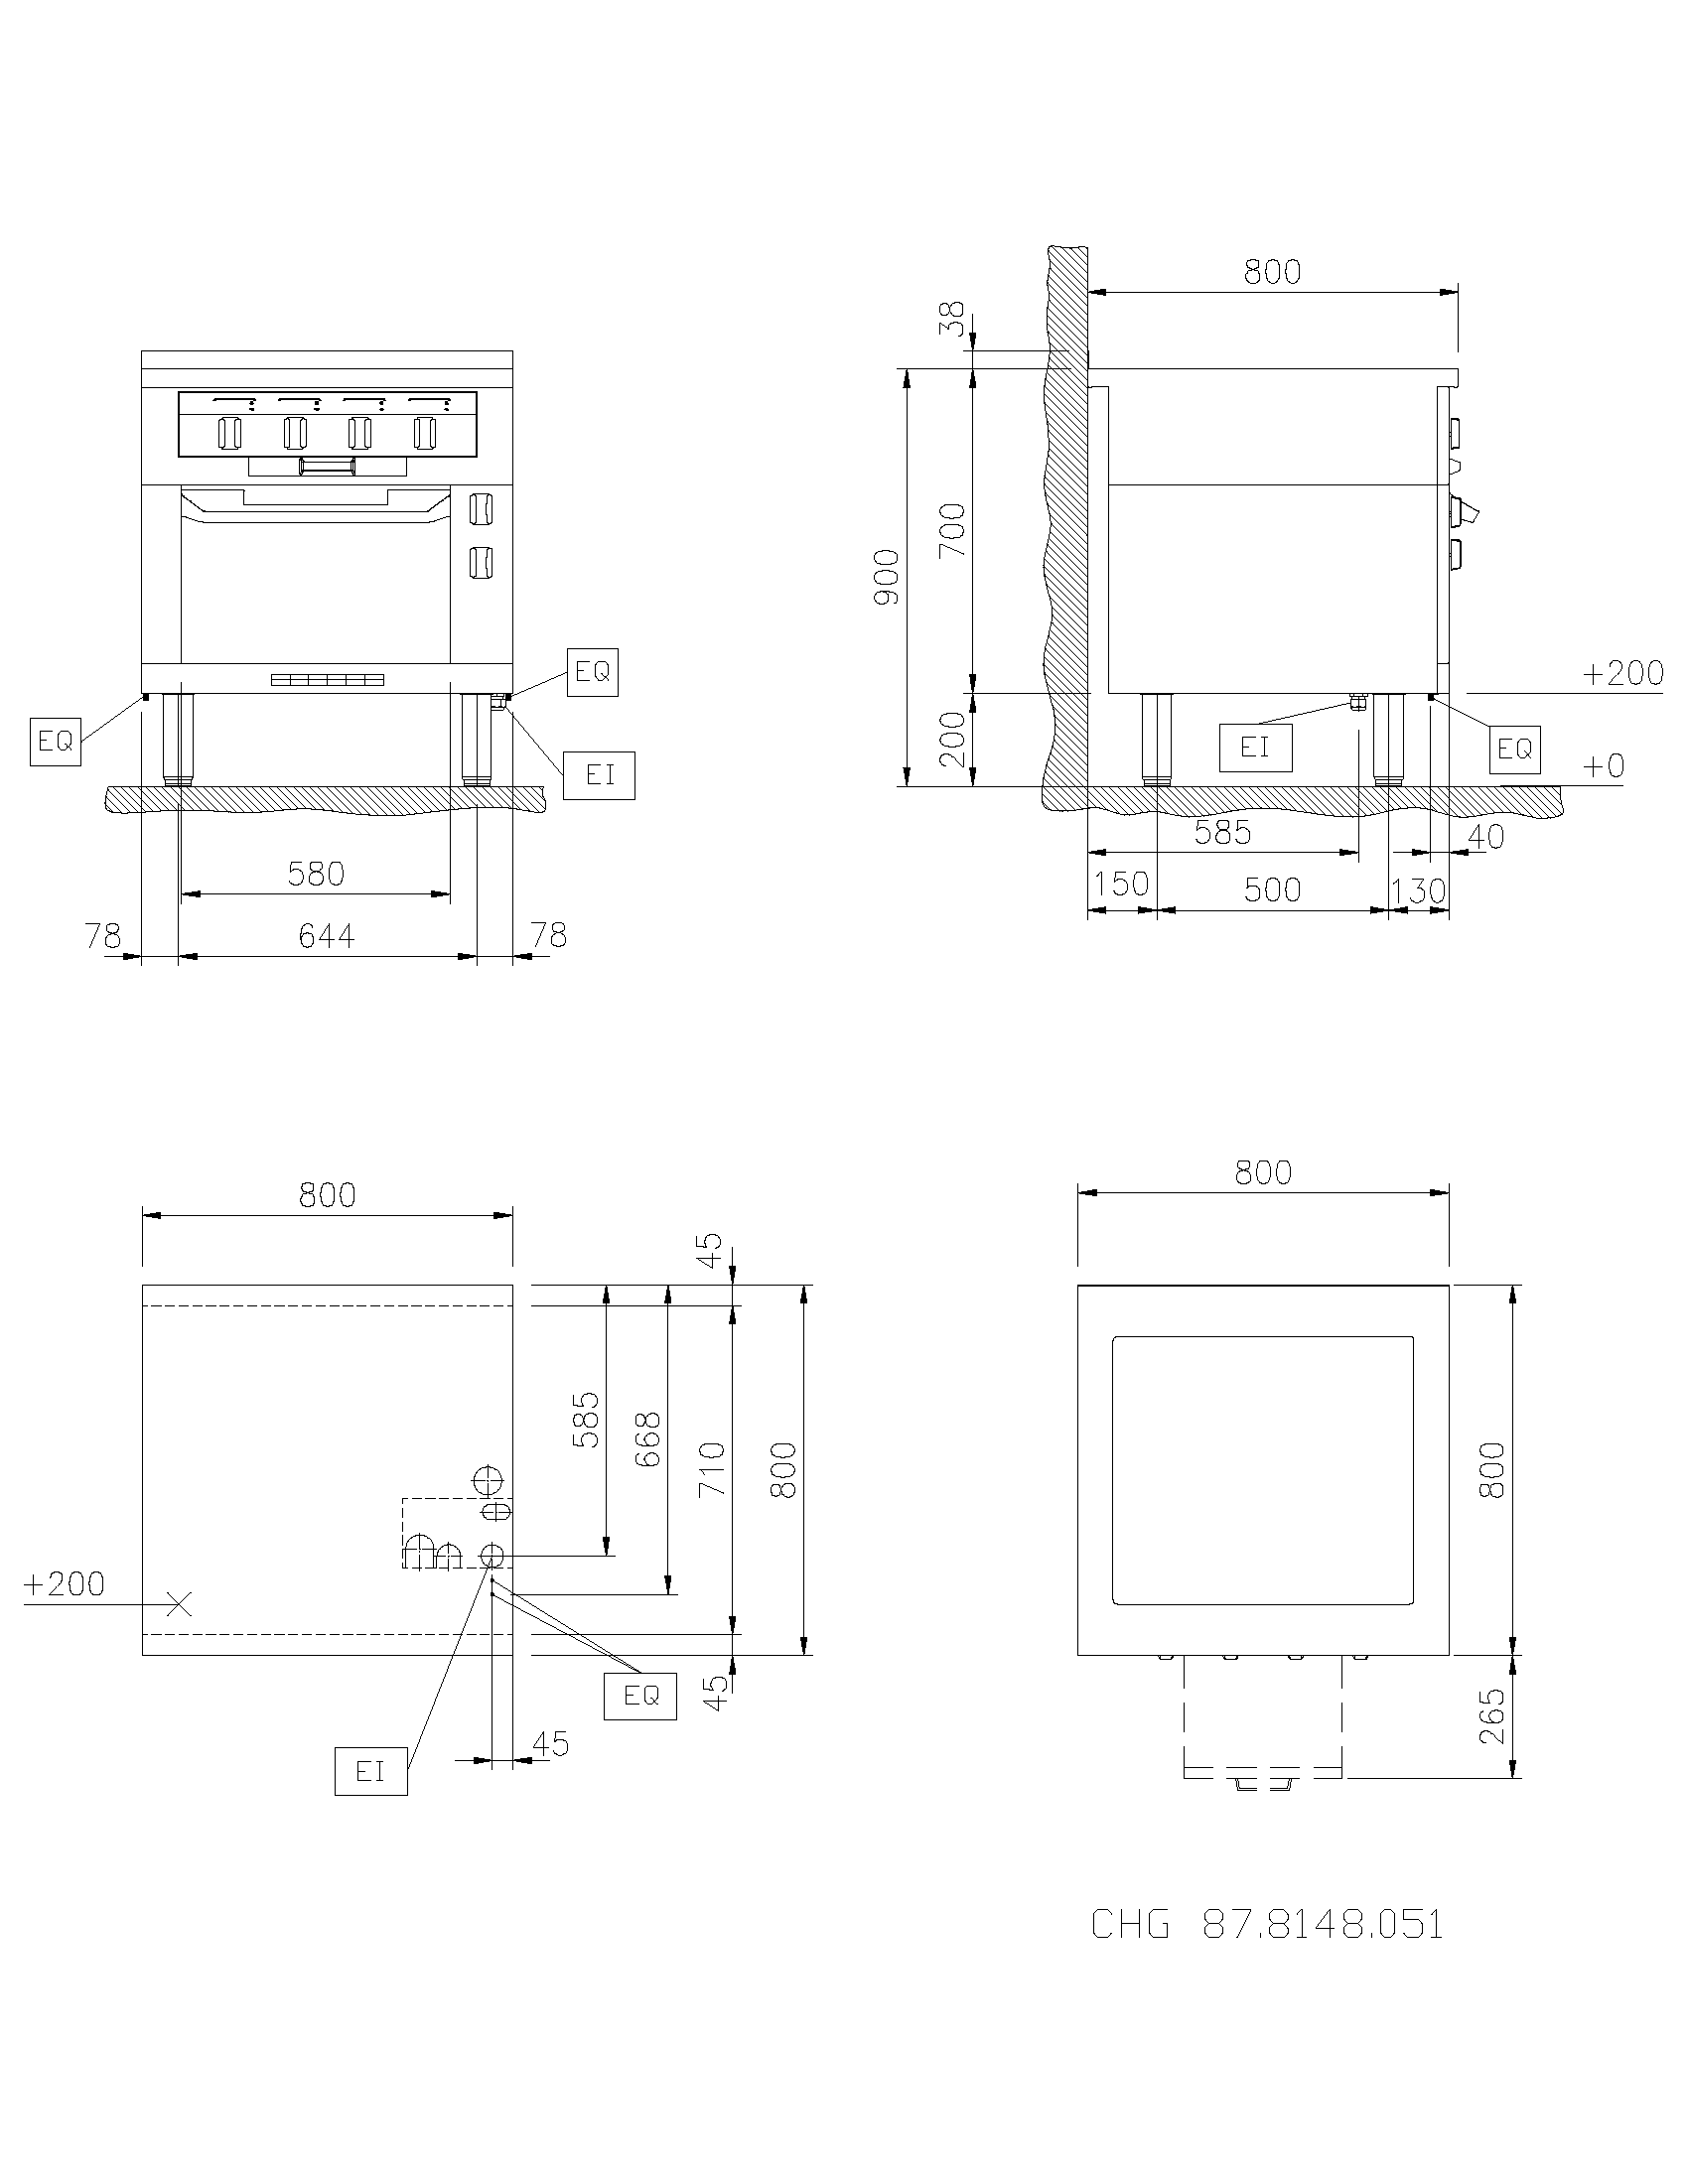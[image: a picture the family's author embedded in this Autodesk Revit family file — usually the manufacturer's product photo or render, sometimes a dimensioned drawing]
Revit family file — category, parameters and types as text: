
# Revit family: QF_ELECTROLUXPROFESSIONAL_588459_MALRECH4AO
name_source: partatom
category: Attrezzature speciali
units: mm (PartAtom-declared; Revit-internal decimal feet)

## family parameters
Basato su piano di lavoro = No
Condiviso = No
Punto di calcolo locali = No
Quota connettore circolare = Usa diametro
Sempre verticale = Sì
Taglio con vuoti quando caricato = No
Tipo di parte = Normale

## types (1)
- Standard
    Accessory = Sì
    Cold Water Size = 0"
    Compressed Air Pressure = 0.00 psi
    Compressed Air Size = 0"
    Compressed Air Volume = 0 GPM
    Condensate Return Size = 0"
    Cycle = 50 Hz
    Depth Actual = 800 mm  [stored 2.62467 ft]
    Descrizione = EL.SOLID TOP,WARM.CAB.PASS,2S,800X800X7
    Direct Waste Size = 0"
    Gas Input Pressure = 0.0
    Gas KW = 0
    Gas Size = 0"
    HP = 19.2 HP
    Height Actual = 700 mm  [stored 2.29659 ft]
    Hot Water Size = 0"
    Item Number = 588459
    Length Actual = 800 mm  [stored 2.62467 ft]
    Modello = MALRECH4AO
    Phase = 3
    Produttore = Electrolux Professional
    Prospetto di default = 0 mm  [stored 0 ft]
    Refrigerant Compressor Remote = Sì
    Refrigeration Liquid Line Size = 0 mm  [stored 0 ft]
    Refrigeration Suction Line Size = 0 mm  [stored 0 ft]
    Steam Consumption per Hour = 0
    Steam Supply Maximum Pressure = 0.00 psi
    Steam Supply Minimum Pressure = 0.00 psi
    Steam Supply Size = 0"
    URL = https://www.electroluxprofessional.com
    URL Manufacturer = https://www.electroluxprofessional.com
    Volts = 400 V
    Watts = 14300 W
    Weight = 147.00 kg

note: source unit labels omitted for Gas Input Pressure — the stored unit's dimension contradicts the parameter name (converter mislabeling)

note: [stored X ft] marks values corroborated as IEEE doubles in the binary element streams (Revit-internal decimal feet)

## geometry (parser evidence)
native form markers: Blend x10, Sweep x15
no freeform markers — native parametric forms only
